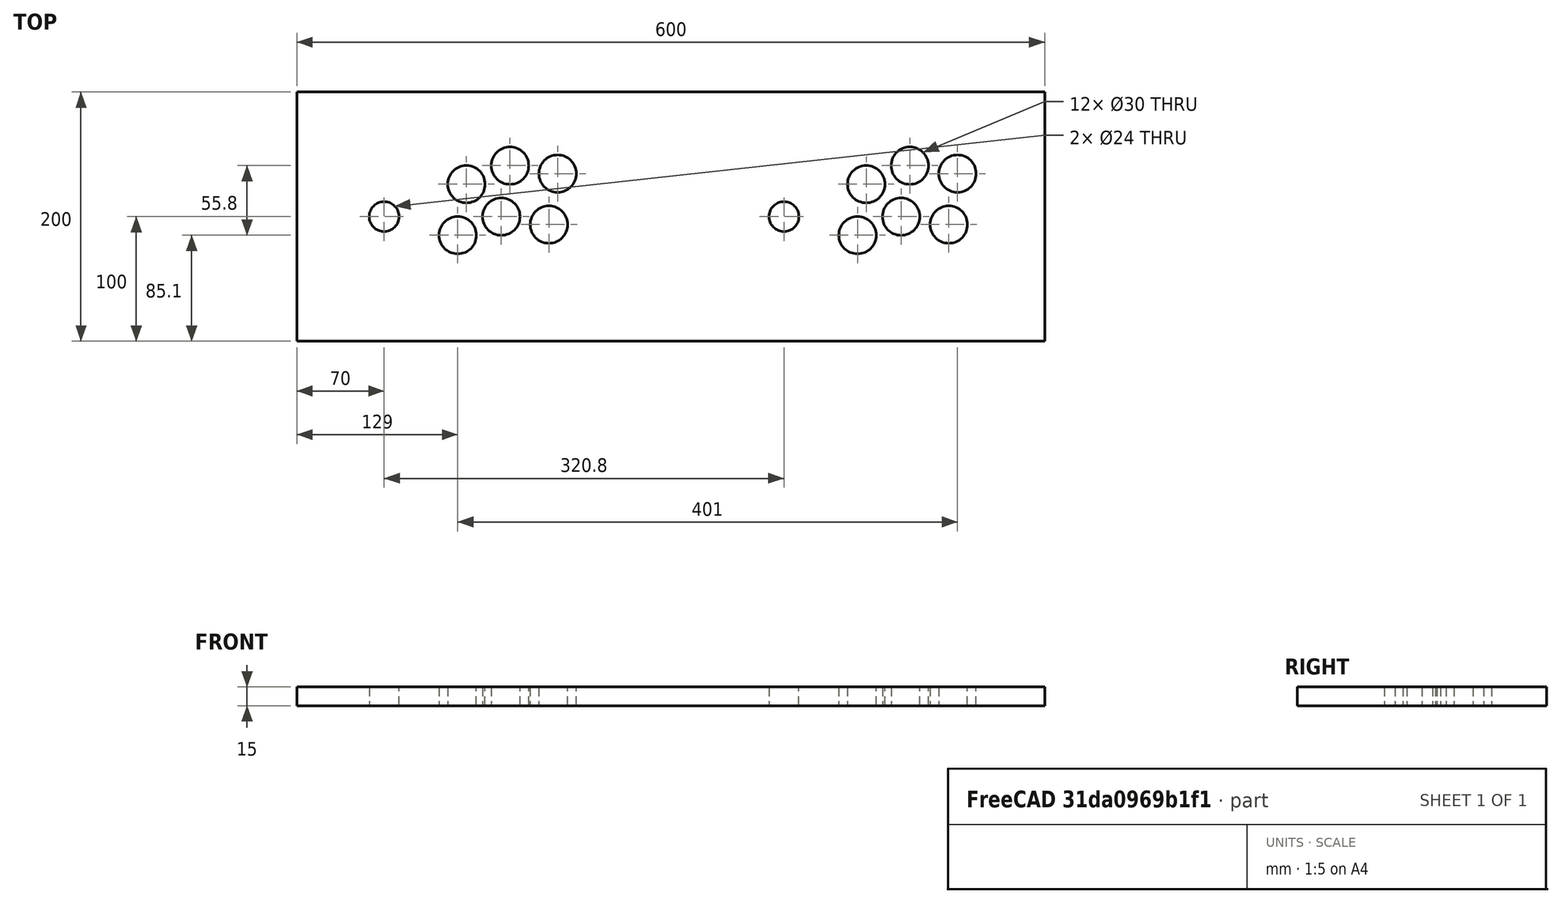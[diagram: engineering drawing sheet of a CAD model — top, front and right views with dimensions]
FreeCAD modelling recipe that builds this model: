
FCSTD DOCUMENT  (FreeCAD 1.0R39319 (Git))
Label: control_panel
License: All rights reserved
LicenseURL: http://fr.wikipedia.org/wiki/<copyright redacted>
objects: Sketcher::SketchObject×1, PartDesign::Pad×1, PartDesign::Body×1
note: 6 computed .brp shape members not serialized (recipe doc carries the construction recipe); baked Part::Feature solids carry a one-line shape summary decoded from their .brp

FEATURE [Sketcher::SketchObject] Sketch  label="control_panel_sketch"
  ArcFitTolerance = 0
  AttachmentSupport = -> [XY_Plane]
  FullyConstrained = true
  MakeInternals = false
  MapMode = 5
  sketch-geometry (23):
    g0: Circle CenterX=70 CenterY=100 CenterZ=0 NormalX=0 NormalY=0 NormalZ=1 AngleXU=0 Radius=12
    g1: Circle CenterX=129 CenterY=85.1 CenterZ=0 NormalX=0 NormalY=0 NormalZ=1 AngleXU=0 Radius=15
    g2: Circle CenterX=164 CenterY=100 CenterZ=0 NormalX=0 NormalY=0 NormalZ=1 AngleXU=0 Radius=15
    g3: Circle CenterX=202.2 CenterY=93.6 CenterZ=0 NormalX=0 NormalY=0 NormalZ=1 AngleXU=0 Radius=15
    g4: Circle CenterX=171 CenterY=140.9 CenterZ=0 NormalX=0 NormalY=0 NormalZ=1 AngleXU=0 Radius=15
    g5: Circle CenterX=209.2 CenterY=134.5 CenterZ=0 NormalX=0 NormalY=0 NormalZ=1 AngleXU=0 Radius=15
    g6: Circle CenterX=136 CenterY=126 CenterZ=0 NormalX=0 NormalY=0 NormalZ=1 AngleXU=0 Radius=15
    g7: LineSegment [constr] StartX=171 StartY=140.9 StartZ=0 EndX=209.2 EndY=134.5 EndZ=0
    g8: LineSegment [constr] StartX=202.2 StartY=93.6 StartZ=0 EndX=164 EndY=100 EndZ=0
    g9: LineSegment StartX=0 StartY=0 StartZ=0 EndX=600 EndY=0 EndZ=0
    g10: LineSegment StartX=600 StartY=0 StartZ=0 EndX=600 EndY=200 EndZ=0
    g11: LineSegment StartX=600 StartY=200 StartZ=0 EndX=0 EndY=200 EndZ=0
    g12: LineSegment StartX=0 StartY=200 StartZ=0 EndX=0 EndY=0 EndZ=0
    g13: Circle CenterX=390.8 CenterY=100 CenterZ=0 NormalX=0 NormalY=0 NormalZ=1 AngleXU=0 Radius=12
    g14: Circle CenterX=449.8 CenterY=85.1 CenterZ=0 NormalX=0 NormalY=0 NormalZ=1 AngleXU=0 Radius=15
    g15: Circle CenterX=484.8 CenterY=100 CenterZ=0 NormalX=0 NormalY=0 NormalZ=1 AngleXU=0 Radius=15
    g16: Circle CenterX=523 CenterY=93.6 CenterZ=0 NormalX=0 NormalY=0 NormalZ=1 AngleXU=0 Radius=15
    g17: Circle CenterX=491.8 CenterY=140.9 CenterZ=0 NormalX=0 NormalY=0 NormalZ=1 AngleXU=0 Radius=15
    g18: Circle CenterX=530 CenterY=134.5 CenterZ=0 NormalX=0 NormalY=0 NormalZ=1 AngleXU=0 Radius=15
    g19: Circle CenterX=456.8 CenterY=126 CenterZ=0 NormalX=0 NormalY=0 NormalZ=1 AngleXU=0 Radius=15
    g20: LineSegment [constr] StartX=491.8 StartY=140.9 StartZ=0 EndX=530 EndY=134.5 EndZ=0
    g21: LineSegment [constr] StartX=523 StartY=93.6 StartZ=0 EndX=484.8 EndY=100 EndZ=0
    g22: LineSegment [constr] StartX=70 StartY=100 StartZ=0 EndX=390.8 EndY=100 EndZ=0
  constraints (63):
    c: Radius(g0) = 12
    c: Radius(g6) = 15
    c: Equal(g6,g4)
    c: Equal(g4,g5)
    c: Equal(g5,g2)
    c: Equal(g2,g3)
    c: Equal(g1,g6)
    c: DistanceX(g0,g1) = 59
    c: DistanceX(g6,g4) = 35
    c: DistanceX(g4,g5) = 38.2
    c: DistanceX(g1,g2) = 35
    c: DistanceX(g2,g3) = 38.2
    c: DistanceX(g0,g6) = 66
    c: DistanceY(g1,g0) = 14.9
    c: DistanceY(g0,g6) = 26
    c: DistanceY(g1,g2) = 14.9
    c: DistanceY(g3,g2) = 6.4
    c: DistanceY(g6,g4) = 14.9
    c: DistanceY(g5,g4) = 6.4
    c: Coincident(g7,g4)
    c: Coincident(g8,g2)
    c: Coincident(g9,g10)
    c: Coincident(g10,g11)
    c: Coincident(g11,g12)
    c: Coincident(g12,g9)
    c: Horizontal(g9)
    c: Horizontal(g11)
    c: Vertical(g10)
    c: Vertical(g12)
    c: Coincident(g9,g-1)
    c: DistanceX(g9,g9) = 600
    c: Equal(g0,g13) = 14
    c: Equal(g6,g19) = 15
    c: Equal(g19,g17)
    c: Equal(g17,g18)
    c: Equal(g18,g15)
    c: Equal(g15,g16)
    c: Equal(g14,g19)
    c: DistanceX(g13,g14) = 59
    c: DistanceX(g19,g17) = 35
    c: DistanceX(g17,g18) = 38.2
    c: DistanceX(g14,g15) = 35
    c: DistanceX(g15,g16) = 38.2
    c: DistanceX(g13,g19) = 66
    c: DistanceY(g14,g13) = 14.9
    c: DistanceY(g13,g19) = 26
    c: DistanceY(g14,g15) = 14.9
    c: DistanceY(g16,g15) = 6.4
    c: DistanceY(g19,g17) = 14.9
    c: DistanceY(g18,g17) = 6.4
    c: Coincident(g20,g17)
    c: Coincident(g21,g15)
    c: DistanceX(g-1,g0) = 70
    c: DistanceY(g12,g12) = 200
    c: DistanceY(g-1,g0) = 100
    c: Coincident(g22,g0)
    c: Coincident(g22,g13)
    c: Horizontal(g22)
    c: Coincident(g21,g16)
    c: Coincident(g20,g18)
    c: Coincident(g8,g3)
    c: Coincident(g7,g5)
    c: DistanceX(g18,g10) = 70
FEATURE [PartDesign::Pad] Pad
  AllowMultiFace = false
  Direction = (0,0,1)
  Length = 15
  Length2 = 100
  Profile = -> Sketch
  ReferenceAxis = -> Sketch [N_Axis]
  Suppressed = false
  Type = 0
FEATURE [PartDesign::Body] Body
  AllowCompound = false
  Group = -> [Sketch,Pad]
  Origin = -> Origin
  Tip = -> Pad
